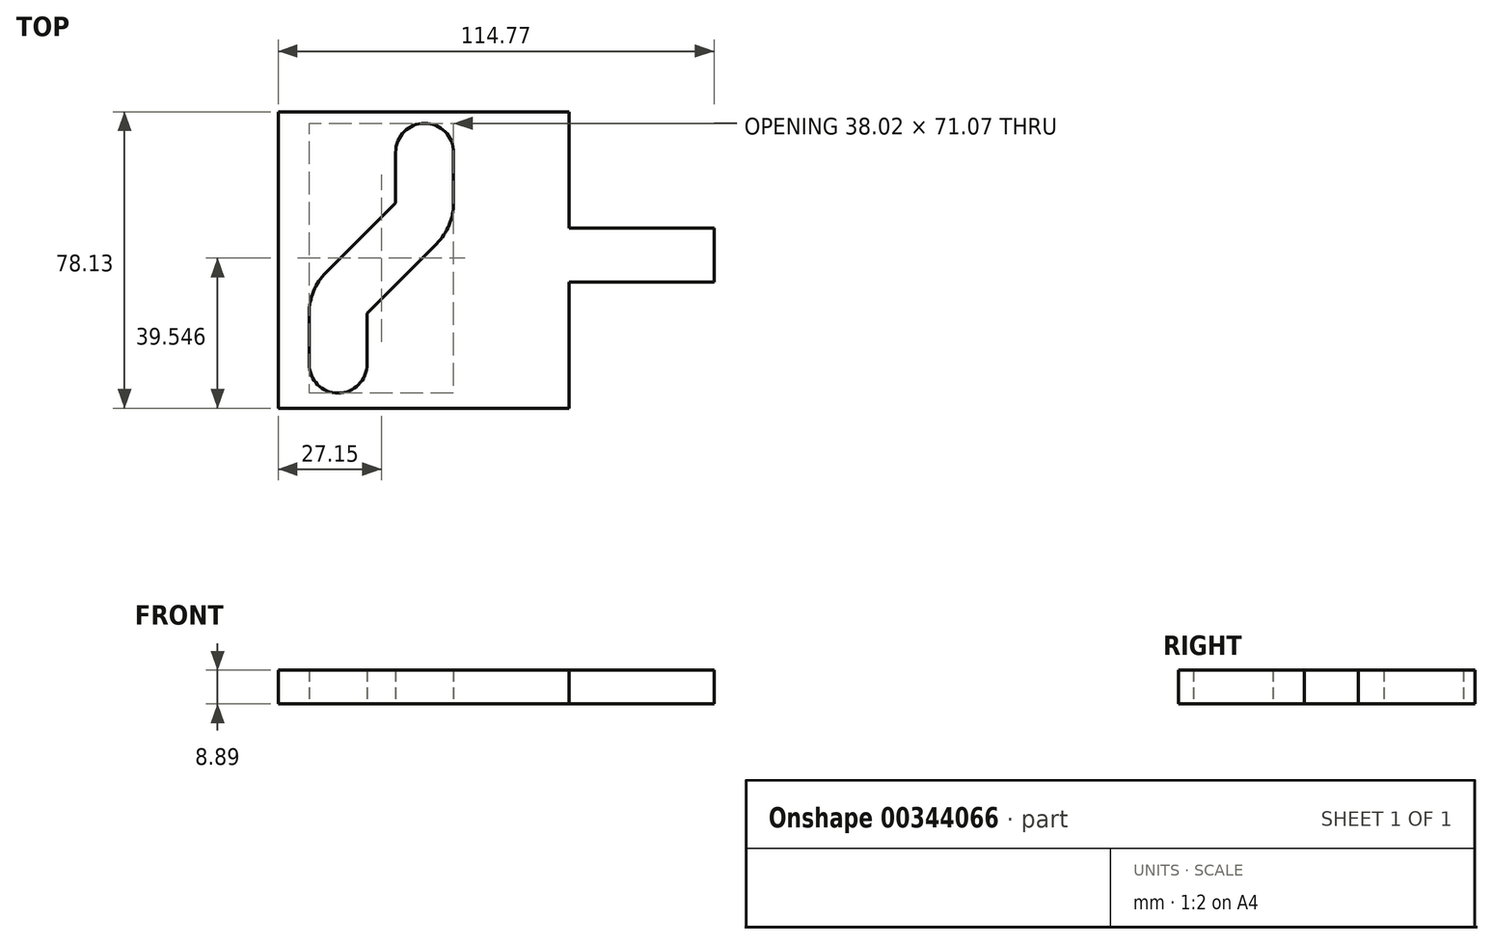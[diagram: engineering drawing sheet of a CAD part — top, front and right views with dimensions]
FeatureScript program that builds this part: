
annotation { "Feature Type Name" : "Feature", "Feature Type Description" : "" }
export const myFeature = defineFeature(function(context is Context, id is Id, definition is map)
    precondition{}
    {
        {
            var Q0;
            Q0=qCreatedBy(makeId("Top.planeOp"),FACE);
            var sketch = newSketch(context, id + "F0", { "sketchPlane" : qUnion([Q0])});
            skLineSegment(sketch, "E0", {"start": v(-10.9, 2.27) * mm, "end": v(-10.9, 53.07) * mm});
            skLineSegment(sketch, "E1", {"start": v(-16.52, 7.93) * mm, "end": v(-7.36, 17.1) * mm});
            skLineSegment(sketch, "E2.MirrorCS", {"start": v(-16.52, 7.88) * mm, "end": v(-25.68, -1.28) * mm});
            skLineSegment(sketch, "E3.MirrorCS", {"start": v(-5.74, -2.84) * mm, "end": v(-14.9, -12) * mm});
            skLineSegment(sketch, "E4", {"start": v(-16.52, 7.93) * mm, "end": v(-25.68, -1.22) * mm});
            skLineSegment(sketch, "E5", {"start": v(-5.74, -2.84) * mm, "end": v(3.42, 6.32) * mm});
            skPoint(sketch, "E6.visualSharp", {"position": v(7.21, 10.1) * mm});
            skArc(sketch, "E6.filletArc", {"start": v(3.42, 6.32) * mm, "mid": v(6.72, 11.26) * mm, "end": v(7.88, 17.1) * mm});
            skPoint(sketch, "E7.visualSharp", {"position": v(-29.47, -5.02) * mm});
            skArc(sketch, "E7.filletArc", {"start": v(-25.68, -1.22) * mm, "mid": v(-28.98, -6.17) * mm, "end": v(-30.14, -12) * mm});
            skLineSegment(sketch, "E8", {"start": v(-7.36, 17.1) * mm, "end": v(-7.36, 30.46) * mm});
            skLineSegment(sketch, "E9.right", {"start": v(-38.28, 4.19) * mm, "end": v(-38.28, 41.13) * mm});
            skLineSegment(sketch, "E10", {"start": v(-38.28, 41.13) * mm, "end": v(38.37, 41.13) * mm});
            skLineSegment(sketch, "E11", {"start": v(7.88, 17.1) * mm, "end": v(7.88, 30.46) * mm});
            skLineSegment(sketch, "E12", {"start": v(-14.9, -12) * mm, "end": v(-14.9, -25.37) * mm});
            skLineSegment(sketch, "E13", {"start": v(-30.14, -12) * mm, "end": v(-30.14, -25.37) * mm});
            skArc(sketch, "E14", {"start": v(7.88, 30.46) * mm, "mid": v(0.26, 38.08) * mm, "end": v(-7.36, 30.46) * mm});
            skArc(sketch, "E15", {"start": v(-30.14, -25.37) * mm, "mid": v(-22.52, -32.99) * mm, "end": v(-14.9, -25.37) * mm});
            skLineSegment(sketch, "E16", {"start": v(76.49, 3.32) * mm, "end": v(76.49, 10.43) * mm});
            skLineSegment(sketch, "E17.MirrorCS", {"start": v(76.49, 3.32) * mm, "end": v(76.49, -3.8) * mm});
            skLineSegment(sketch, "E18", {"start": v(76.49, -3.8) * mm, "end": v(38.37, -3.8) * mm});
            skLineSegment(sketch, "E19", {"start": v(76.49, 10.43) * mm, "end": v(38.37, 10.43) * mm});
            skLineSegment(sketch, "E20", {"start": v(38.37, 41.13) * mm, "end": v(38.37, 10.43) * mm});
            skLineSegment(sketch, "E21", {"start": v(-38.28, 4.19) * mm, "end": v(-38.28, -37) * mm});
            skLineSegment(sketch, "E22", {"start": v(38.37, -3.8) * mm, "end": v(38.37, -37) * mm});
            skLineSegment(sketch, "E23", {"start": v(-38.28, -37) * mm, "end": v(38.37, -37) * mm});
            skSolve(sketch);
        }
        {
            var Q0;
            Q0=makeQuery(id+"F0.imprint","IMPRINT",FACE,{"disambiguationData":[TD([[makeQuery(id+"F0.imprint","IMPRINT",EDGE,{"derivedFrom":sQuery(id+"F0.wireOp",EDGE,"E3.MirrorCS")}),1.0]])]});
            extrude(context, id + "F1", {"entities" : qUnion([Q0]), "depth" : 8.9 * mm});
        }
    });
